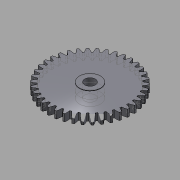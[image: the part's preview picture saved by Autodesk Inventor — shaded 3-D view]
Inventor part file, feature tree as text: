
AUTODESK INVENTOR PART (.ipt)
format: ipt  version: 2015 (Build 190159000, 159)  size: 335,360 bytes
history: native  units: in
note: dims shown in document units (in); Inventor stores cm internally (conversion verified against a paired STEP export)
features: other x13, sketch x5, plane x2
ambient origin geometry x8: Origin, YZ Plane, XZ Plane, XY Plane, X Axis, Y Axis, Z Axis, Center Point
bodies: Solid1 (feature_tree)
feature tree (20):
  other  "Spur Gear2"
  other  "Solid1::Spur Gear2"
  other  "TaggingFeature1"
  sketch  "Sketch1"  dims[d0=0.3937in]
  sketch  "Sketch2"  dims[d16=0.5709in d17=0.0in d41=0.0in d43=0.5709in d46=0.5709in d47=0.0in d48=0.0in]
  sketch  "Sketch3"
  sketch  "Sketch4"
  sketch  "Sketch5"
  plane  "XZ Plane_1"
  plane  "Work Plane2"
  other  "Z Axis_1"
  other  "Srf1"
  other  "Srf1::Derived"
  other  "Distance iMate"
  other  "Align iMate"
  other  "Mesh iMate"
  other  "Axis iMate"
  other  "Position iMate"
  other  "Mesh iMate2"
  other  "Start plane iMate"
